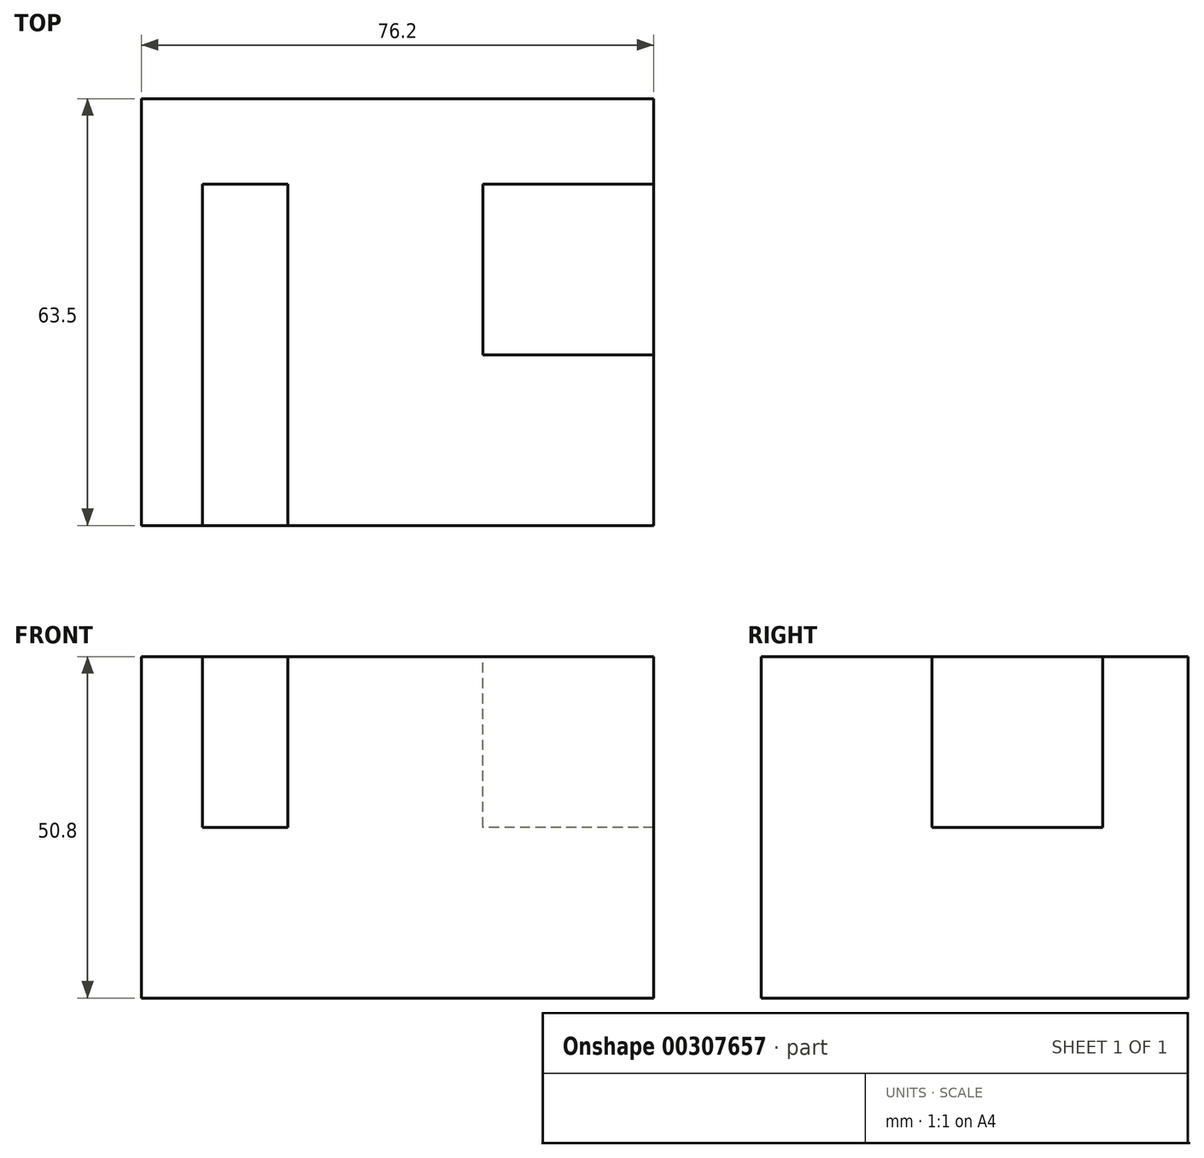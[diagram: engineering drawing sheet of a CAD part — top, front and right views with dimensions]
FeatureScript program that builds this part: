
annotation { "Feature Type Name" : "Feature", "Feature Type Description" : "" }
export const myFeature = defineFeature(function(context is Context, id is Id, definition is map)
    precondition{}
    {
        {
            var Q0;
            Q0=qCreatedBy(makeId("Front.planeOp"),FACE);
            var sketch = newSketch(context, id + "F0", { "sketchPlane" : qUnion([Q0])});
            skLineSegment(sketch, "E0", {"start": v(-29.73, 28.7) * mm, "end": v(46.47, 28.7) * mm});
            skLineSegment(sketch, "E1", {"start": v(46.47, 28.7) * mm, "end": v(46.47, -22.1) * mm});
            skLineSegment(sketch, "E2", {"start": v(-29.73, 28.7) * mm, "end": v(-29.73, -22.1) * mm});
            skLineSegment(sketch, "E3", {"start": v(-29.73, -22.1) * mm, "end": v(46.47, -22.1) * mm});
            skSolve(sketch);
        }
        {
            var Q0;
            Q0 = qSketchRegion(id + "F0", true);
            extrude(context, id + "F1", {"entities" : qUnion([Q0]), "depth" : 63.5 * mm});
        }
        {
            var Q0;
            Q0=makeQuery(id+"F1.opExtrude","SWEPT_FACE",FACE,{"disambiguationData":[OSD([sQuery(id+"F0.wireOp",EDGE,"E0")])]});
            var sketch = newSketch(context, id + "F2", { "sketchPlane" : qUnion([Q0])});
            skLineSegment(sketch, "E4.bottom", {"start": v(-20.68, -63.5) * mm, "end": v(-7.98, -63.5) * mm});
            skLineSegment(sketch, "E4.top", {"start": v(-20.68, -12.7) * mm, "end": v(-7.98, -12.7) * mm});
            skLineSegment(sketch, "E4.left", {"start": v(-20.68, -63.5) * mm, "end": v(-20.68, -12.7) * mm});
            skLineSegment(sketch, "E4.right", {"start": v(-7.98, -63.5) * mm, "end": v(-7.98, -12.7) * mm});
            skSolve(sketch);
        }
        {
            var Q0;
            Q0=makeQuery(id+"F2.imprint","IMPRINT",FACE,{"disambiguationData":[TD([[makeQuery(id+"F2.imprint","IMPRINT",EDGE,{"derivedFrom":sQuery(id+"F2.wireOp",EDGE,"E4.bottom")}),1.0]])]});
            extrude(context, id + "F3", {"entities" : qUnion([Q0]), "operationType" : NewBodyOperationType.REMOVE, "oppositeDirection" : true, "depth" : 25.4 * mm});
        }
        {
            var Q0;
            Q0=makeQuery(id+"F1.opExtrude","SWEPT_FACE",FACE,{"disambiguationData":[OSD([sQuery(id+"F0.wireOp",EDGE,"E0")])]});
            var sketch = newSketch(context, id + "F4", { "sketchPlane" : qUnion([Q0])});
            skLineSegment(sketch, "E5.bottom", {"start": v(46.47, -12.7) * mm, "end": v(21.07, -12.7) * mm});
            skLineSegment(sketch, "E5.top", {"start": v(46.47, -38.1) * mm, "end": v(21.07, -38.1) * mm});
            skLineSegment(sketch, "E5.left", {"start": v(46.47, -12.7) * mm, "end": v(46.47, -38.1) * mm});
            skLineSegment(sketch, "E5.right", {"start": v(21.07, -12.7) * mm, "end": v(21.07, -38.1) * mm});
            skSolve(sketch);
        }
        {
            var Q0;
            Q0 = qSketchRegion(id + "F4", true);
            extrude(context, id + "F5", {"entities" : qUnion([Q0]), "operationType" : NewBodyOperationType.REMOVE, "oppositeDirection" : true, "depth" : 25.4 * mm});
        }
    });
